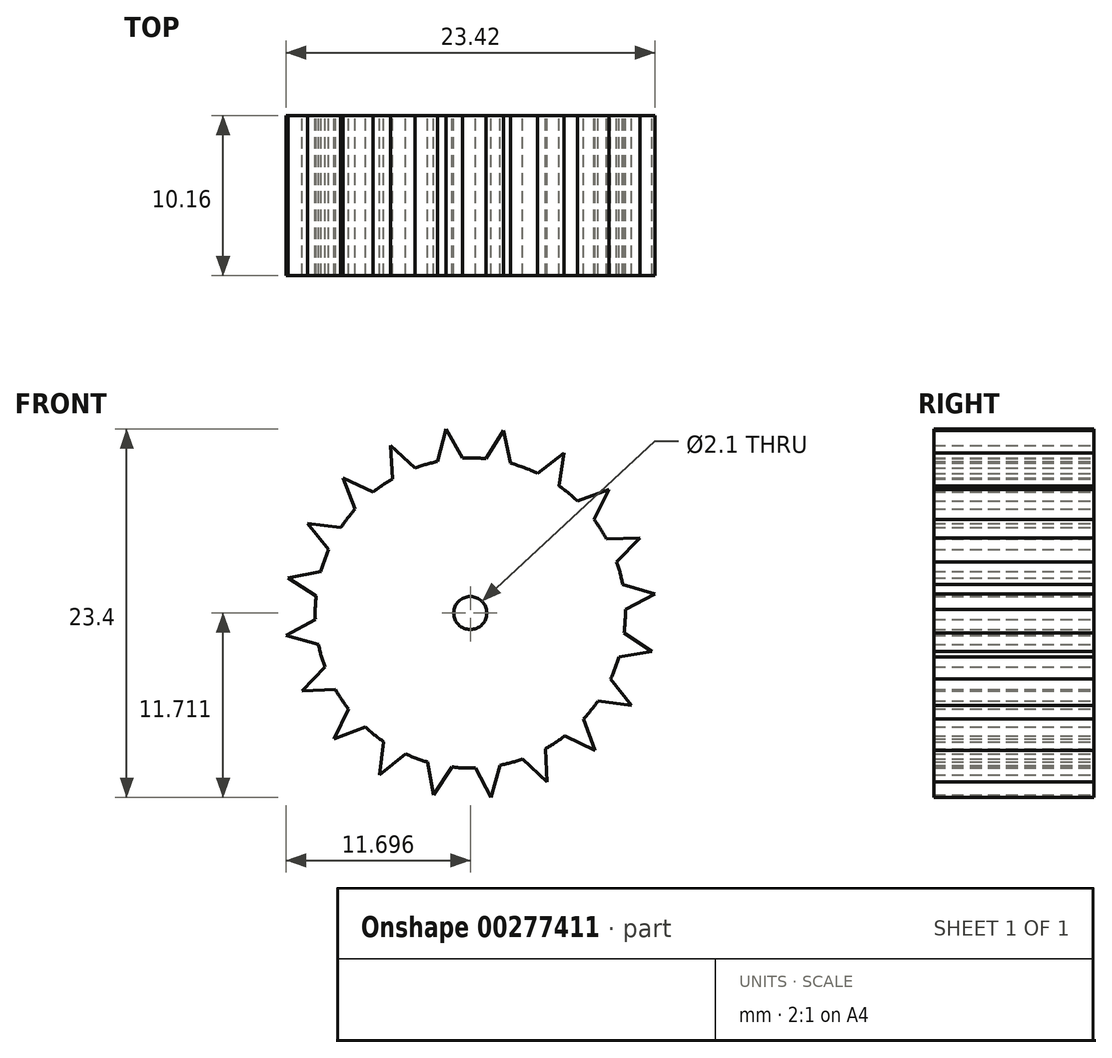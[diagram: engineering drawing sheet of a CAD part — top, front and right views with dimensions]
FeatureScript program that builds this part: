
annotation { "Feature Type Name" : "Feature", "Feature Type Description" : "" }
export const myFeature = defineFeature(function(context is Context, id is Id, definition is map)
    precondition{}
    {
        {
            var Q0;
            Q0=qCreatedBy(makeId("Front.planeOp"),FACE);
            var sketch = newSketch(context, id + "F0", { "sketchPlane" : qUnion([Q0])});
            skCircle(sketch, "E0", {"center": v(-46.8, 23.94) * mm, "radius": 9.85 * mm});
            skLineSegment(sketch, "E1", {"start": v(-42.51, 32.81) * mm, "end": v(-40.84, 34.11) * mm});
            skLineSegment(sketch, "E2", {"start": v(-41.15, 32.01) * mm, "end": v(-40.84, 34.11) * mm});
            skLineSegment(sketch, "E3.1.0", {"start": v(-40, 31.07) * mm, "end": v(-38, 31.79) * mm});
            skLineSegment(sketch, "E3.1.1", {"start": v(-38.94, 29.89) * mm, "end": v(-38, 31.79) * mm});
            skLineSegment(sketch, "E3.2.0", {"start": v(-38.13, 28.63) * mm, "end": v(-36.01, 28.7) * mm});
            skLineSegment(sketch, "E3.2.1", {"start": v(-37.5, 27.19) * mm, "end": v(-36.01, 28.7) * mm});
            skLineSegment(sketch, "E3.3.0", {"start": v(-37.11, 25.74) * mm, "end": v(-35.07, 25.16) * mm});
            skLineSegment(sketch, "E3.3.1", {"start": v(-36.95, 24.17) * mm, "end": v(-35.07, 25.16) * mm});
            skLineSegment(sketch, "E3.4.0", {"start": v(-37.03, 22.68) * mm, "end": v(-35.26, 21.5) * mm});
            skLineSegment(sketch, "E3.4.1", {"start": v(-37.35, 21.14) * mm, "end": v(-35.26, 21.5) * mm});
            skLineSegment(sketch, "E3.5.0", {"start": v(-37.88, 19.74) * mm, "end": v(-36.57, 18.08) * mm});
            skLineSegment(sketch, "E3.5.1", {"start": v(-38.67, 18.37) * mm, "end": v(-36.57, 18.08) * mm});
            skLineSegment(sketch, "E3.6.0", {"start": v(-39.6, 17.2) * mm, "end": v(-38.87, 15.22) * mm});
            skLineSegment(sketch, "E3.6.1", {"start": v(-40.77, 16.14) * mm, "end": v(-38.87, 15.22) * mm});
            skLineSegment(sketch, "E3.7.0", {"start": v(-42.02, 15.32) * mm, "end": v(-41.93, 13.2) * mm});
            skLineSegment(sketch, "E3.7.1", {"start": v(-43.46, 14.67) * mm, "end": v(-41.93, 13.2) * mm});
            skLineSegment(sketch, "E3.8.0", {"start": v(-44.9, 14.28) * mm, "end": v(-45.46, 12.23) * mm});
            skLineSegment(sketch, "E3.8.1", {"start": v(-46.47, 14.1) * mm, "end": v(-45.46, 12.23) * mm});
            skLineSegment(sketch, "E3.9.0", {"start": v(-47.96, 14.16) * mm, "end": v(-49.13, 12.39) * mm});
            skLineSegment(sketch, "E3.9.1", {"start": v(-49.51, 14.47) * mm, "end": v(-49.13, 12.39) * mm});
            skLineSegment(sketch, "E3.10.0", {"start": v(-50.91, 15) * mm, "end": v(-52.56, 13.66) * mm});
            skLineSegment(sketch, "E3.10.1", {"start": v(-52.29, 15.77) * mm, "end": v(-52.56, 13.66) * mm});
            skLineSegment(sketch, "E3.11.0", {"start": v(-53.46, 16.7) * mm, "end": v(-55.44, 15.93) * mm});
            skLineSegment(sketch, "E3.11.1", {"start": v(-54.53, 17.85) * mm, "end": v(-55.44, 15.93) * mm});
            skLineSegment(sketch, "E3.12.0", {"start": v(-55.37, 19.1) * mm, "end": v(-57.48, 18.98) * mm});
            skLineSegment(sketch, "E3.12.1", {"start": v(-56.03, 20.52) * mm, "end": v(-57.48, 18.98) * mm});
            skLineSegment(sketch, "E3.13.0", {"start": v(-56.44, 21.96) * mm, "end": v(-58.5, 22.5) * mm});
            skLineSegment(sketch, "E3.13.1", {"start": v(-56.63, 23.53) * mm, "end": v(-58.5, 22.5) * mm});
            skLineSegment(sketch, "E3.14.0", {"start": v(-56.58, 25.02) * mm, "end": v(-58.37, 26.17) * mm});
            skLineSegment(sketch, "E3.14.1", {"start": v(-56.29, 26.57) * mm, "end": v(-58.37, 26.17) * mm});
            skLineSegment(sketch, "E3.15.0", {"start": v(-55.78, 27.98) * mm, "end": v(-57.12, 29.62) * mm});
            skLineSegment(sketch, "E3.15.1", {"start": v(-55.02, 29.36) * mm, "end": v(-57.12, 29.62) * mm});
            skLineSegment(sketch, "E3.16.0", {"start": v(-54.1, 30.54) * mm, "end": v(-54.88, 32.52) * mm});
            skLineSegment(sketch, "E3.16.1", {"start": v(-52.96, 31.62) * mm, "end": v(-54.88, 32.52) * mm});
            skLineSegment(sketch, "E3.17.0", {"start": v(-51.72, 32.47) * mm, "end": v(-51.85, 34.59) * mm});
            skLineSegment(sketch, "E3.17.1", {"start": v(-50.3, 33.15) * mm, "end": v(-51.85, 34.59) * mm});
            skLineSegment(sketch, "E3.18.0", {"start": v(-48.86, 33.57) * mm, "end": v(-48.34, 35.63) * mm});
            skLineSegment(sketch, "E3.18.1", {"start": v(-47.3, 33.78) * mm, "end": v(-48.34, 35.63) * mm});
            skLineSegment(sketch, "E3.19.0", {"start": v(-45.8, 33.74) * mm, "end": v(-44.67, 35.54) * mm});
            skLineSegment(sketch, "E3.19.1", {"start": v(-44.25, 33.46) * mm, "end": v(-44.67, 35.54) * mm});
            skLineSegment(sketch, "E3.anchor1", {"start": v(-46.8, 23.94) * mm, "end": v(-42.51, 32.81) * mm, "construction": true});
            skLineSegment(sketch, "E3.anchor2", {"start": v(-46.8, 23.94) * mm, "end": v(-45.8, 33.74) * mm, "construction": true});
            skCircle(sketch, "E4", {"center": v(-46.8, 23.94) * mm, "radius": 1.05 * mm});
            skSolve(sketch);
        }
        {
            var Q0;
            Q0 = qSketchRegion(id + "F0", true);
            extrude(context, id + "F1", {"entities" : qUnion([Q0]), "depth" : 5.08 * mm, "hasSecondDirection" : true, "secondDirectionOppositeDirection" : true, "secondDirectionDepth" : 5.08 * mm});
        }
    });
